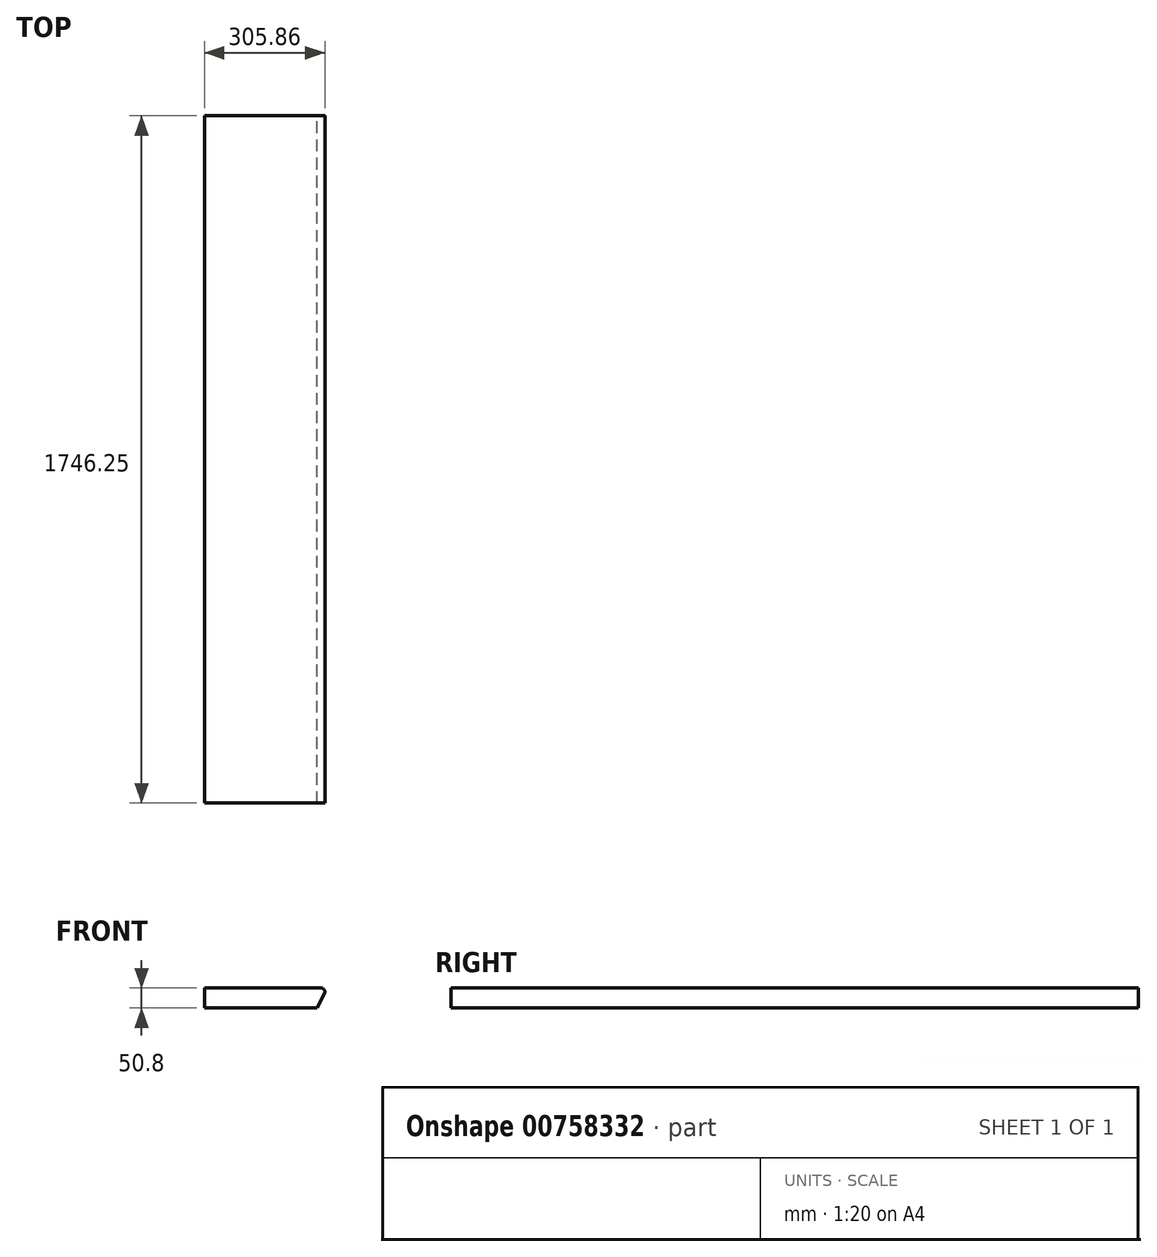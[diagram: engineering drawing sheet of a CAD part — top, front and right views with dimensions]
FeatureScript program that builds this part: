
annotation { "Feature Type Name" : "Feature", "Feature Type Description" : "" }
export const myFeature = defineFeature(function(context is Context, id is Id, definition is map)
    precondition{}
    {
        {
            var Q0;
            Q0=qCreatedBy(makeId("Front.planeOp"),FACE);
            var sketch = newSketch(context, id + "F0", { "sketchPlane" : qUnion([Q0])});
            skLineSegment(sketch, "E0", {"start": v(-275.83, 0) * mm, "end": v(-275.83, 50.8) * mm});
            skLineSegment(sketch, "E1", {"start": v(-275.83, 50.8) * mm, "end": v(20.5, 50.8) * mm});
            skLineSegment(sketch, "E2", {"start": v(28.97, 36.9) * mm, "end": v(9.92, 0) * mm});
            skLineSegment(sketch, "E3", {"start": v(9.92, 0) * mm, "end": v(-275.83, 0) * mm});
            skArc(sketch, "E4.filletArc", {"start": v(28.97, 36.9) * mm, "mid": v(28.64, 46.23) * mm, "end": v(20.5, 50.8) * mm});
            skSolve(sketch);
        }
        {
            var Q0;
            Q0=makeQuery(id+"F0.imprint","IMPRINT",FACE,{"disambiguationData":[TD([[makeQuery(id+"F0.imprint","IMPRINT",EDGE,{"derivedFrom":sQuery(id+"F0.wireOp",EDGE,"E0")}),-1.0]])]});
            extrude(context, id + "F1", {"entities" : qUnion([Q0]), "depth" : 1746.25 * mm, "offsetDistance" : 25.4 * mm});
        }
    });
